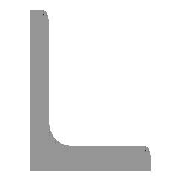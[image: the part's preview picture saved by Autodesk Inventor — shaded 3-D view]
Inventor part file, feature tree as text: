
AUTODESK INVENTOR PART (.ipt)
format: ipt  version: 2016 (Build 200138000, 138)  size: 122,880 bytes
history: native  units: mm (DEFAULTED — no unit token found)
features: other x4, sketch x3, plane x2, extrude x1
ambient origin geometry x8: Origin, YZ Plane, XZ Plane, XY Plane, X Axis, Y Axis, Z Axis, Center Point
bodies: Solid1 (feature_tree)
feature tree (10):
  parser-record x1  (decoder bookkeeping rows leaked as tree rows — omitted from the tree; the rows remain in map.json)
  other  "Driven Length"
  other  "Plano inicial"
  other  "Plano final"
  extrude  "Cuerpo"  Depth=38.1mm
  sketch  "Boceto5"  dims[d3=4.7625mm d4=2400.0mm d5=0.0mm d10=0.0mm d11=0.0mm d12=-0.0mm d13=2400.0mm d14=4.826mm d15=2.286mm d16=90.0deg d17=2400.0mm]
  plane  "Plano de trabajo4"
  sketch  "Sketch3"  dims[d0=38.1mm d1=38.1mm]
  plane  "Work Plane3"
  sketch  "Sketch4"  dims[d2=4.7625mm]
